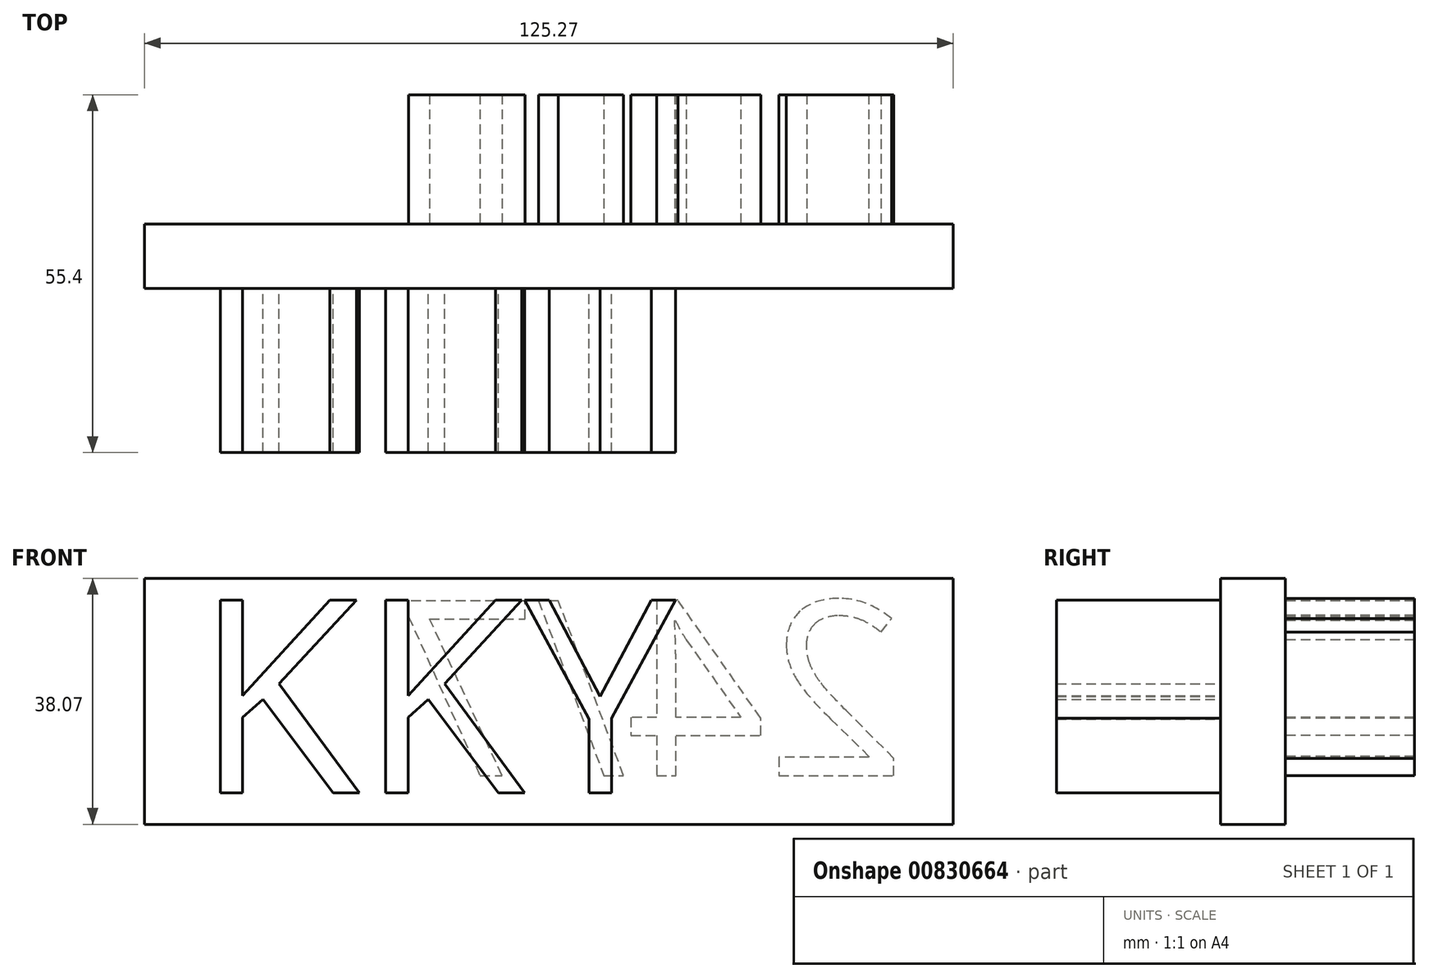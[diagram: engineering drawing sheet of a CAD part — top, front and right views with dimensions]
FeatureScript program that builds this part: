
annotation { "Feature Type Name" : "Feature", "Feature Type Description" : "" }
export const myFeature = defineFeature(function(context is Context, id is Id, definition is map)
    precondition{}
    {
        {
            var Q0;
            Q0=qCreatedBy(makeId("Front.planeOp"),FACE);
            var sketch = newSketch(context, id + "F0", { "sketchPlane" : qUnion([Q0])});
            skLineSegment(sketch, "E0.bottom", {"start": v(0, 0) * mm, "end": v(125.27, 0) * mm});
            skLineSegment(sketch, "E0.top", {"start": v(0, 38.07) * mm, "end": v(125.27, 38.07) * mm});
            skLineSegment(sketch, "E0.left", {"start": v(0, 0) * mm, "end": v(0, 38.07) * mm});
            skLineSegment(sketch, "E0.right", {"start": v(125.27, 0) * mm, "end": v(125.27, 38.07) * mm});
            skSolve(sketch);
        }
        {
            var Q0;
            Q0 = qSketchRegion(id + "F0", true);
            extrude(context, id + "F1", {"entities" : qUnion([Q0]), "depth" : 10 * mm, "offsetDistance" : 25.4 * mm});
        }
        {
            var Q0;
            Q0=makeQuery(id+"F1.opExtrude","CAP_FACE",FACE,{"disambiguationData":[OSD([sQuery(id+"F0.wireOp",EDGE,"E0.bottom"),sQuery(id+"F0.wireOp",EDGE,"E0.top"),sQuery(id+"F0.wireOp",EDGE,"E0.left"),sQuery(id+"F0.wireOp",EDGE,"E0.right")])],"isStart":false});
            var sketch = newSketch(context, id + "F2", { "sketchPlane" : qUnion([Q0])});
            skSolve(sketch);
        }
        {
            var Q0;
            Q0=makeQuery(id+"F2.imprint","IMPRINT",FACE,{"disambiguationData":[TD([[makeQuery(id+"F2.imprint","IMPRINT",EDGE,{"derivedFrom":makeQuery(id+"F1.opExtrude","CAP_EDGE",EDGE,{"disambiguationData":[OSD([sQuery(id+"F0.wireOp",EDGE,"E0.bottom")])],"isStart":false})}),1.0]])]});
            var sketch = newSketch(context, id + "F3", { "sketchPlane" : qUnion([Q0])});
            skText(sketch, "E1", { "text": "KKY", "fontName": "OpenSans-Regular.ttf"});
            const initialGuessF3  = {"E1": [0.00767, 0.00489, 1, 0, 0.03005]};
            skSetInitialGuess(sketch, initialGuessF3);
            skSolve(sketch);
        }
        {
            var Q0;
            Q0 = qSketchRegion(id + "F3", true);
            extrude(context, id + "F4", {"entities" : qUnion([Q0]), "operationType" : NewBodyOperationType.ADD, "depth" : 25.4 * mm, "offsetDistance" : 25.4 * mm});
        }
        {
            var Q0;
            Q0=makeQuery(id+"F1.opExtrude","CAP_FACE",FACE,{"disambiguationData":[OSD([sQuery(id+"F0.wireOp",EDGE,"E0.bottom"),sQuery(id+"F0.wireOp",EDGE,"E0.top"),sQuery(id+"F0.wireOp",EDGE,"E0.left"),sQuery(id+"F0.wireOp",EDGE,"E0.right")])],"isStart":true});
            var sketch = newSketch(context, id + "F5", { "sketchPlane" : qUnion([Q0])});
            skText(sketch, "E2", { "text": "24/7", "fontName": "OpenSans-Regular.ttf"});
            const initialGuessF5  = {"E2": [-0.1179, 0.00754, 1, 0, 0.02728]};
            skSetInitialGuess(sketch, initialGuessF5);
            skSolve(sketch);
        }
        {
            var Q0;
            Q0 = qSketchRegion(id + "F5", true);
            extrude(context, id + "F6", {"entities" : qUnion([Q0]), "operationType" : NewBodyOperationType.ADD, "depth" : 20 * mm, "offsetDistance" : 25.4 * mm});
        }
    });
